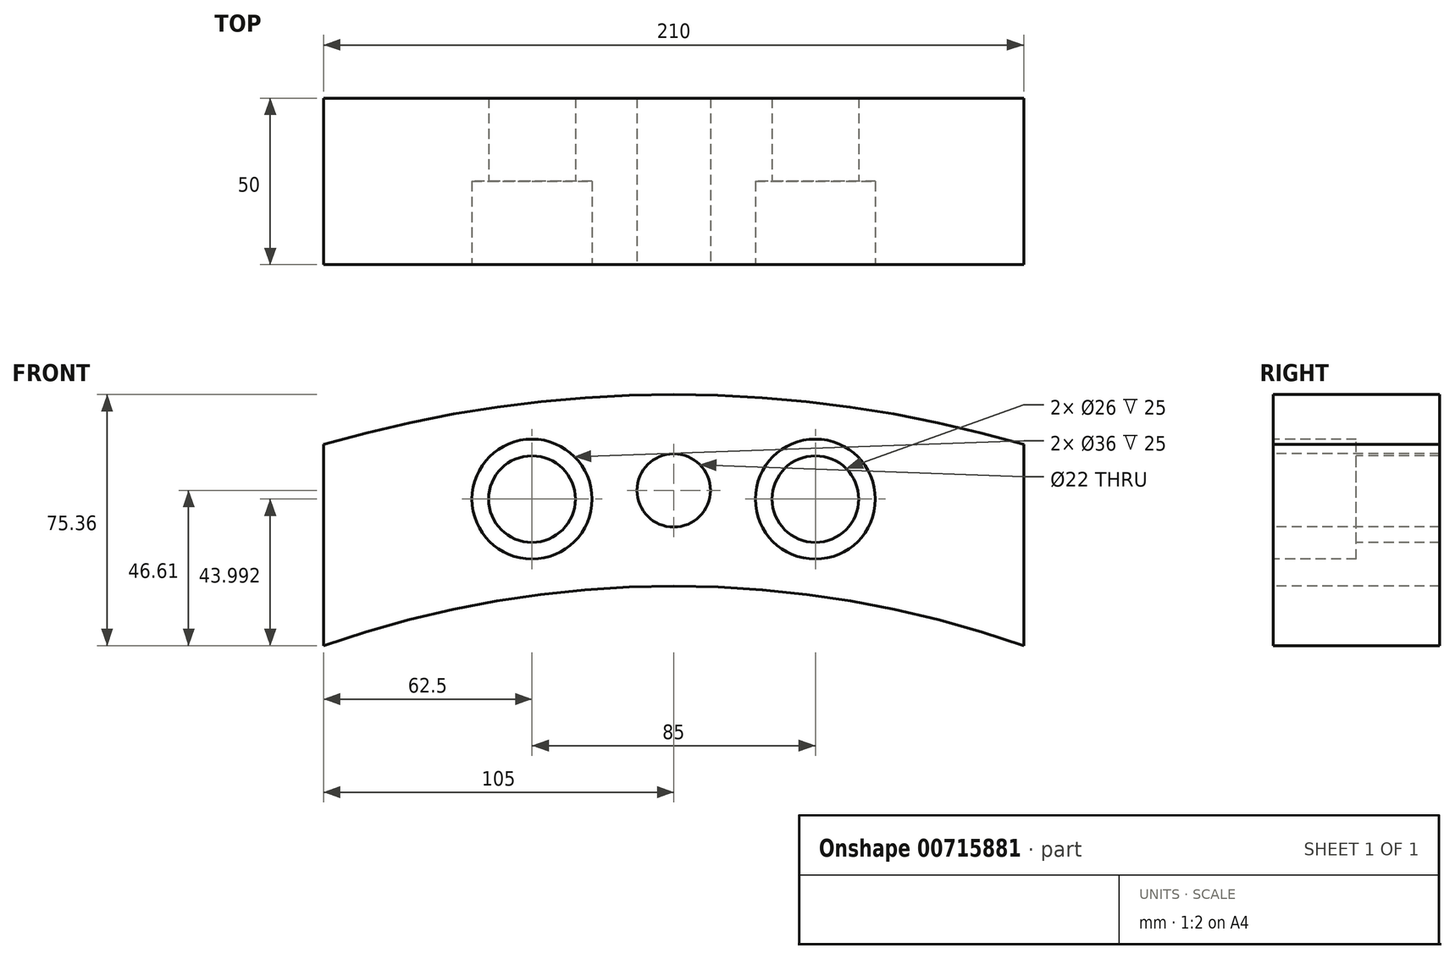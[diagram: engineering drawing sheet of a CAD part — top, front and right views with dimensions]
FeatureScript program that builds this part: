
annotation { "Feature Type Name" : "Feature", "Feature Type Description" : "" }
export const myFeature = defineFeature(function(context is Context, id is Id, definition is map)
    precondition{}
    {
        {
            var Q0;
            Q0=qCreatedBy(makeId("Front.planeOp"),FACE);
            var sketch = newSketch(context, id + "F0", { "sketchPlane" : qUnion([Q0])});
            skCircle(sketch, "E0", {"center": v(0, 0) * mm, "radius": 317.5 * mm});
            skCircle(sketch, "E1", {"center": v(0, 0) * mm, "radius": 375 * mm});
            skLineSegment(sketch, "E2.bottom", {"start": v(-105, 456.66) * mm, "end": v(105, 456.66) * mm});
            skLineSegment(sketch, "E2.top", {"start": v(-105, 256.66) * mm, "end": v(105, 256.66) * mm});
            skLineSegment(sketch, "E2.left", {"start": v(-105, 456.66) * mm, "end": v(-105, 256.66) * mm});
            skLineSegment(sketch, "E2.right", {"start": v(105, 456.66) * mm, "end": v(105, 256.66) * mm});
            skLineSegment(sketch, "E3", {"start": v(0, 0) * mm, "end": v(0, 466.73) * mm, "construction": true});
            skCircle(sketch, "E4", {"center": v(0, 346.25) * mm, "radius": 11 * mm});
            skCircle(sketch, "E5", {"center": v(0, 0) * mm, "radius": 346.25 * mm});
            skCircle(sketch, "E6", {"center": v(-42.5, 343.63) * mm, "radius": 13 * mm});
            skCircle(sketch, "E7", {"center": v(42.5, 343.63) * mm, "radius": 13 * mm});
            skCircle(sketch, "E8", {"center": v(-42.5, 343.63) * mm, "radius": 18 * mm});
            skCircle(sketch, "E9", {"center": v(42.5, 343.63) * mm, "radius": 18 * mm});
            skSolve(sketch);
        }
        {
            var Q0;
            {var subQ5=sQuery(id+"F0.wireOp",EDGE,"E1");var subQ8=sQuery(id+"F0.wireOp",EDGE,"E2.left");var subQ12=makeQuery(id+"F0.imprint","INTERSECT",VERTEX,{"derivedFrom":[subQ5,subQ8]});Q0=makeQuery(id+"F0.imprint","IMPRINT",FACE,{"disambiguationData":[TD([[makeQuery(id+"F0.imprint","IMPRINT",EDGE,{"disambiguationData":[TD([[subQ12,1.0]])],"derivedFrom":subQ5}),1.0]])]});}
            var Q1;
            {var subQ8=sQuery(id+"F0.wireOp",EDGE,"E0");var subQ11=sQuery(id+"F0.wireOp",EDGE,"E2.left");var subQ12=makeQuery(id+"F0.imprint","INTERSECT",VERTEX,{"derivedFrom":[subQ8,subQ11]});Q1=makeQuery(id+"F0.imprint","IMPRINT",FACE,{"disambiguationData":[TD([[makeQuery(id+"F0.imprint","IMPRINT",EDGE,{"disambiguationData":[TD([[subQ12,1.0]])],"derivedFrom":subQ8}),-1.0]])]});}
            var Q2;
            {var subQ0=sQuery(id+"F0.wireOp",EDGE,"E8");var subQ1=sQuery(id+"F0.wireOp",EDGE,"E5");var subQ2=makeQuery(id+"F0.imprint","INTERSECT",VERTEX,{"disambiguationData":[OD(0.0)],"derivedFrom":[subQ1,subQ0]});Q2=makeQuery(id+"F0.imprint","IMPRINT",FACE,{"disambiguationData":[TD([[makeQuery(id+"F0.imprint","IMPRINT",EDGE,{"disambiguationData":[TD([[subQ2,-1.0]])],"derivedFrom":subQ1}),-1.0]])]});}
            var Q3;
            {var subQ0=sQuery(id+"F0.wireOp",EDGE,"E8");var subQ1=sQuery(id+"F0.wireOp",EDGE,"E5");var subQ2=makeQuery(id+"F0.imprint","INTERSECT",VERTEX,{"disambiguationData":[OD(0.0)],"derivedFrom":[subQ1,subQ0]});Q3=makeQuery(id+"F0.imprint","IMPRINT",FACE,{"disambiguationData":[TD([[makeQuery(id+"F0.imprint","IMPRINT",EDGE,{"disambiguationData":[TD([[subQ2,-1.0]])],"derivedFrom":subQ1}),1.0]])]});}
            var Q4;
            {var subQ0=sQuery(id+"F0.wireOp",EDGE,"E9");var subQ1=sQuery(id+"F0.wireOp",EDGE,"E5");var subQ2=makeQuery(id+"F0.imprint","INTERSECT",VERTEX,{"disambiguationData":[OD(0.0)],"derivedFrom":[subQ1,subQ0]});Q4=makeQuery(id+"F0.imprint","IMPRINT",FACE,{"disambiguationData":[TD([[makeQuery(id+"F0.imprint","IMPRINT",EDGE,{"disambiguationData":[TD([[subQ2,-1.0]])],"derivedFrom":subQ1}),-1.0]])]});}
            var Q5;
            {var subQ0=sQuery(id+"F0.wireOp",EDGE,"E9");var subQ1=sQuery(id+"F0.wireOp",EDGE,"E5");var subQ2=makeQuery(id+"F0.imprint","INTERSECT",VERTEX,{"disambiguationData":[OD(0.0)],"derivedFrom":[subQ1,subQ0]});Q5=makeQuery(id+"F0.imprint","IMPRINT",FACE,{"disambiguationData":[TD([[makeQuery(id+"F0.imprint","IMPRINT",EDGE,{"disambiguationData":[TD([[subQ2,-1.0]])],"derivedFrom":subQ1}),1.0]])]});}
            extrude(context, id + "F1", {"entities" : qUnion([Q0, Q1, Q2, Q3, Q4, Q5]), "oppositeDirection" : true, "depth" : 50 * mm, "offsetDistance" : 25 * mm});
        }
        {
            var Q0;
            {var subQ0=sQuery(id+"F0.wireOp",EDGE,"E8");var subQ1=sQuery(id+"F0.wireOp",EDGE,"E5");var subQ2=makeQuery(id+"F0.imprint","INTERSECT",VERTEX,{"disambiguationData":[OD(0.0)],"derivedFrom":[subQ1,subQ0]});Q0=makeQuery(id+"F0.imprint","IMPRINT",FACE,{"disambiguationData":[TD([[makeQuery(id+"F0.imprint","IMPRINT",EDGE,{"disambiguationData":[TD([[subQ2,-1.0]])],"derivedFrom":subQ1}),-1.0]])]});}
            var Q1;
            {var subQ0=sQuery(id+"F0.wireOp",EDGE,"E8");var subQ1=sQuery(id+"F0.wireOp",EDGE,"E5");var subQ2=makeQuery(id+"F0.imprint","INTERSECT",VERTEX,{"disambiguationData":[OD(0.0)],"derivedFrom":[subQ1,subQ0]});Q1=makeQuery(id+"F0.imprint","IMPRINT",FACE,{"disambiguationData":[TD([[makeQuery(id+"F0.imprint","IMPRINT",EDGE,{"disambiguationData":[TD([[subQ2,-1.0]])],"derivedFrom":subQ1}),1.0]])]});}
            var Q2;
            {var subQ0=sQuery(id+"F0.wireOp",EDGE,"E9");var subQ1=sQuery(id+"F0.wireOp",EDGE,"E5");var subQ2=makeQuery(id+"F0.imprint","INTERSECT",VERTEX,{"disambiguationData":[OD(0.0)],"derivedFrom":[subQ1,subQ0]});Q2=makeQuery(id+"F0.imprint","IMPRINT",FACE,{"disambiguationData":[TD([[makeQuery(id+"F0.imprint","IMPRINT",EDGE,{"disambiguationData":[TD([[subQ2,-1.0]])],"derivedFrom":subQ1}),-1.0]])]});}
            var Q3;
            {var subQ0=sQuery(id+"F0.wireOp",EDGE,"E9");var subQ1=sQuery(id+"F0.wireOp",EDGE,"E5");var subQ2=makeQuery(id+"F0.imprint","INTERSECT",VERTEX,{"disambiguationData":[OD(0.0)],"derivedFrom":[subQ1,subQ0]});Q3=makeQuery(id+"F0.imprint","IMPRINT",FACE,{"disambiguationData":[TD([[makeQuery(id+"F0.imprint","IMPRINT",EDGE,{"disambiguationData":[TD([[subQ2,-1.0]])],"derivedFrom":subQ1}),1.0]])]});}
            extrude(context, id + "F2", {"entities" : qUnion([Q0, Q1, Q2, Q3]), "operationType" : NewBodyOperationType.REMOVE, "oppositeDirection" : true, "depth" : 25 * mm, "offsetDistance" : 25 * mm});
        }
    });
